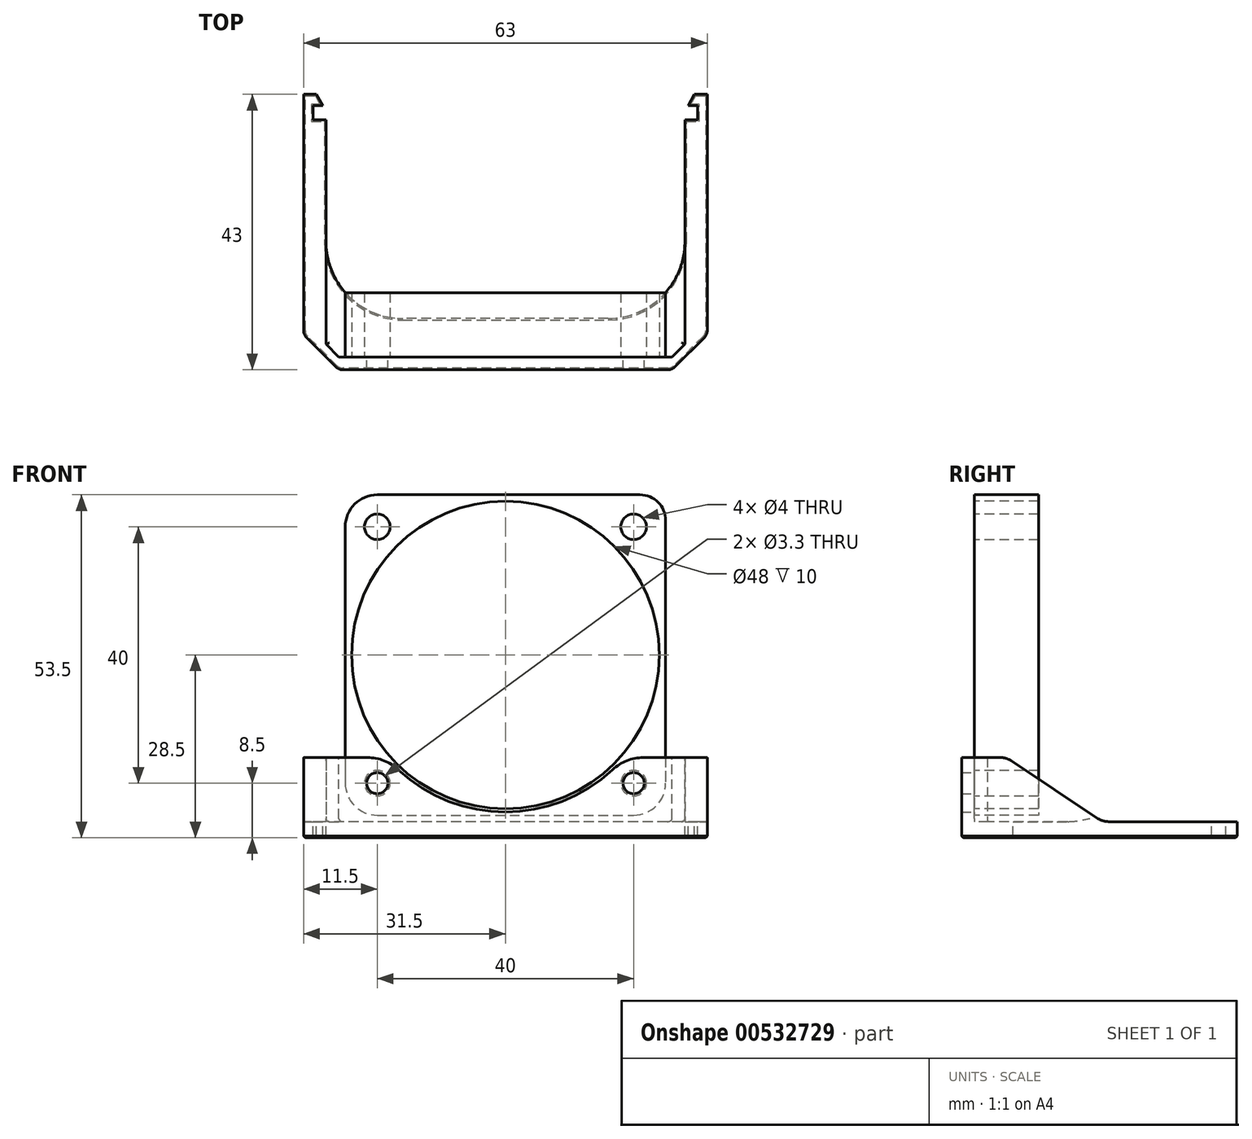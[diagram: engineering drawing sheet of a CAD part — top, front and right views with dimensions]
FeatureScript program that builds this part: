
annotation { "Feature Type Name" : "Feature", "Feature Type Description" : "" }
export const myFeature = defineFeature(function(context is Context, id is Id, definition is map)
    precondition{}
    {
        {
            var Q0;
            Q0=qCreatedBy(makeId("Front.planeOp"),FACE);
            var sketch = newSketch(context, id + "F0", { "sketchPlane" : qUnion([Q0])});
            skLineSegment(sketch, "E0.bottom", {"start": v(-20, 25) * mm, "end": v(21, 25) * mm});
            skLineSegment(sketch, "E0.top", {"start": v(-20, -25) * mm, "end": v(20, -25) * mm});
            skLineSegment(sketch, "E0.left", {"start": v(-25, 20) * mm, "end": v(-25, -20) * mm});
            skLineSegment(sketch, "E0.right", {"start": v(25, 21) * mm, "end": v(25, -20) * mm});
            skPoint(sketch, "E0.middle", {"position": v(0, 0) * mm});
            skCircle(sketch, "E1", {"center": v(20, 20) * mm, "radius": 2 * mm});
            skCircle(sketch, "E2", {"center": v(-20, 20) * mm, "radius": 2 * mm});
            skCircle(sketch, "E3", {"center": v(20, -20) * mm, "radius": 2 * mm});
            skCircle(sketch, "E4", {"center": v(-20, -20) * mm, "radius": 2 * mm});
            skLineSegment(sketch, "E5", {"start": v(20, 20) * mm, "end": v(-20, -20) * mm, "construction": true});
            skLineSegment(sketch, "E6", {"start": v(-20, 20) * mm, "end": v(20, -20) * mm, "construction": true});
            skPoint(sketch, "E7.visualSharp", {"position": v(-25, 25) * mm});
            skArc(sketch, "E7.filletArc", {"start": v(-20, 25) * mm, "mid": v(-23.54, 23.54) * mm, "end": v(-25, 20) * mm});
            skPoint(sketch, "E8.visualSharp", {"position": v(-25, -25) * mm});
            skArc(sketch, "E8.filletArc", {"start": v(-25, -20) * mm, "mid": v(-23.54, -23.54) * mm, "end": v(-20, -25) * mm});
            skPoint(sketch, "E9.visualSharp", {"position": v(25, -25) * mm});
            skArc(sketch, "E9.filletArc", {"start": v(20, -25) * mm, "mid": v(23.54, -23.54) * mm, "end": v(25, -20) * mm});
            skPoint(sketch, "E10.visualSharp", {"position": v(25, 25) * mm});
            skArc(sketch, "E10.filletArc", {"start": v(25, 21) * mm, "mid": v(23.83, 23.83) * mm, "end": v(21, 25) * mm});
            skCircle(sketch, "E11", {"center": v(0, 0) * mm, "radius": 24 * mm});
            skSolve(sketch);
        }
        {
            var Q0;
            Q0=makeQuery(id+"F0.imprint","IMPRINT",FACE,{"disambiguationData":[TD([[makeQuery(id+"F0.imprint","IMPRINT",EDGE,{"derivedFrom":sQuery(id+"F0.wireOp",EDGE,"E0.bottom")}),-1.0]])]});
            extrude(context, id + "F1", {"entities" : qUnion([Q0]), "oppositeDirection" : true, "depth" : 10 * mm, "offsetDistance" : 25 * mm});
        }
        {
            var Q0;
            Q0=makeQuery(id+"F0.imprint","IMPRINT",FACE,{"disambiguationData":[TD([[makeQuery(id+"F0.imprint","IMPRINT",EDGE,{"derivedFrom":sQuery(id+"F0.wireOp",EDGE,"E11")}),1.0]])]});
            var sketch = newSketch(context, id + "F2", { "sketchPlane" : qUnion([Q0])});
            skLineSegment(sketch, "E12", {"start": v(26, -26) * mm, "end": v(-26, -26) * mm});
            skLineSegment(sketch, "E13", {"start": v(-26, -26) * mm, "end": v(-26, -16) * mm});
            skLineSegment(sketch, "E14", {"start": v(26, -26) * mm, "end": v(26, -16) * mm});
            skPoint(sketch, "E15", {"position": v(0, -26) * mm});
            skLineSegment(sketch, "E16", {"start": v(-26, -16) * mm, "end": v(-18.55, -16) * mm});
            skLineSegment(sketch, "E17", {"start": v(26, -16) * mm, "end": v(18.55, -16) * mm});
            skArc(sketch, "E18", {"start": v(-18.55, -16) * mm, "mid": v(0, -24.5) * mm, "end": v(18.55, -16) * mm});
            skArc(sketch, "E19", {"start": v(18.55, -16) * mm, "mid": v(0, 24.5) * mm, "end": v(-18.55, -16) * mm, "construction": true});
            skCircle(sketch, "E20", {"center": v(-20, -20) * mm, "radius": 1.65 * mm});
            skCircle(sketch, "E21", {"center": v(20, -20) * mm, "radius": 1.65 * mm});
            skSolve(sketch);
        }
        {
            var Q0;
            Q0 = qSketchRegion(id + "F2", true);
            extrude(context, id + "F3", {"entities" : qUnion([Q0]), "depth" : 2 * mm, "offsetDistance" : 25 * mm});
        }
        {
            var Q0;
            Q0=makeQuery(id+"F3.opExtrude","SWEPT_FACE",FACE,{"disambiguationData":[OSD([sQuery(id+"F2.wireOp",EDGE,"E12")])]});
            var sketch = newSketch(context, id + "F4", { "sketchPlane" : qUnion([Q0])});
            skLineSegment(sketch, "E22", {"start": v(-31.5, -37) * mm, "end": v(-31.5, -3.5) * mm});
            skLineSegment(sketch, "E23", {"start": v(0, 0) * mm, "end": v(0, -40.2) * mm, "construction": true});
            skLineSegment(sketch, "E24", {"start": v(0, 2) * mm, "end": v(0, -6) * mm});
            skLineSegment(sketch, "E25", {"start": v(0, -6) * mm, "end": v(-16, -6) * mm});
            skLineSegment(sketch, "E26", {"start": v(-28, -18) * mm, "end": v(-28, -37) * mm});
            skLineSegment(sketch, "E27", {"start": v(-26, 2) * mm, "end": v(-31.5, -3.5) * mm});
            skLineSegment(sketch, "E28", {"start": v(-31.5, -37) * mm, "end": v(-31.5, -41) * mm});
            skLineSegment(sketch, "E29", {"start": v(-31.5, -41) * mm, "end": v(-29.5, -41) * mm});
            skLineSegment(sketch, "E30", {"start": v(-29.5, -41) * mm, "end": v(-28.5, -39.2) * mm});
            skLineSegment(sketch, "E31", {"start": v(-28.5, -39.2) * mm, "end": v(-30, -39.2) * mm});
            skLineSegment(sketch, "E32", {"start": v(-30, -39.2) * mm, "end": v(-30, -37) * mm});
            skLineSegment(sketch, "E33", {"start": v(-30, -37) * mm, "end": v(-28, -37) * mm});
            skPoint(sketch, "E34.visualSharp", {"position": v(-28, -6) * mm});
            skArc(sketch, "E34.filletArc", {"start": v(-16, -6) * mm, "mid": v(-24.49, -9.51) * mm, "end": v(-28, -18) * mm});
            skLineSegment(sketch, "E35", {"start": v(-26, 2) * mm, "end": v(0, 2) * mm});
            skPoint(sketch, "E36.orphan", {"position": v(-31.5, 2) * mm});
            skLineSegment(sketch, "E37.MirrorCS", {"start": v(29.5, -41) * mm, "end": v(28.5, -39.2) * mm});
            skLineSegment(sketch, "E38.MirrorCS", {"start": v(31.5, -41) * mm, "end": v(29.5, -41) * mm});
            skLineSegment(sketch, "E39.MirrorCS", {"start": v(30, -37) * mm, "end": v(28, -37) * mm});
            skLineSegment(sketch, "E40.MirrorCS", {"start": v(28.5, -39.2) * mm, "end": v(30, -39.2) * mm});
            skLineSegment(sketch, "E41.MirrorCS", {"start": v(30, -39.2) * mm, "end": v(30, -37) * mm});
            skLineSegment(sketch, "E42.MirrorCS", {"start": v(31.5, -37) * mm, "end": v(31.5, -3.5) * mm});
            skPoint(sketch, "E43.MirrorP", {"position": v(31.5, 2) * mm});
            skLineSegment(sketch, "E44.MirrorCS", {"start": v(0, -6) * mm, "end": v(16, -6) * mm});
            skPoint(sketch, "E45.MirrorP", {"position": v(28, -6) * mm});
            skLineSegment(sketch, "E46.MirrorCS", {"start": v(26, 2) * mm, "end": v(31.5, -3.5) * mm});
            skLineSegment(sketch, "E47.MirrorCS", {"start": v(26, 2) * mm, "end": v(0, 2) * mm});
            skLineSegment(sketch, "E48.MirrorCS", {"start": v(28, -18) * mm, "end": v(28, -37) * mm});
            skLineSegment(sketch, "E49.MirrorCS", {"start": v(31.5, -37) * mm, "end": v(31.5, -41) * mm});
            skArc(sketch, "E50.MirrorCS", {"start": v(16, -6) * mm, "mid": v(24.49, -9.51) * mm, "end": v(28, -18) * mm});
            skSolve(sketch);
        }
        {
            var Q0;
            Q0 = qSketchRegion(id + "F4", true);
            extrude(context, id + "F5", {"entities" : qUnion([Q0]), "operationType" : NewBodyOperationType.ADD, "depth" : 2.5 * mm, "offsetDistance" : 25 * mm});
        }
        {
            var Q0;
            Q0=makeQuery(id+"F4.imprint","IMPRINT",FACE,{"disambiguationData":[TD([[makeQuery(id+"F4.imprint","IMPRINT",EDGE,{"derivedFrom":sQuery(id+"F4.wireOp",EDGE,"E37.MirrorCS")}),-1.0]])]});
            var sketch = newSketch(context, id + "F6", { "sketchPlane" : qUnion([Q0])});
            skLineSegment(sketch, "E51", {"start": v(-26, 2) * mm, "end": v(-31.5, -3.5) * mm});
            skLineSegment(sketch, "E52", {"start": v(-31.5, -3.5) * mm, "end": v(-31.5, -20) * mm});
            skLineSegment(sketch, "E53", {"start": v(-31.5, -20) * mm, "end": v(-28, -20) * mm});
            skLineSegment(sketch, "E54", {"start": v(-28, -20) * mm, "end": v(-28, -2) * mm});
            skLineSegment(sketch, "E55", {"start": v(-28, -2) * mm, "end": v(-26, 0) * mm});
            skLineSegment(sketch, "E56", {"start": v(-26, 0) * mm, "end": v(-26, 2) * mm});
            skLineSegment(sketch, "E57.MirrorCS", {"start": v(26, 0) * mm, "end": v(26, 2) * mm});
            skLineSegment(sketch, "E58.MirrorCS", {"start": v(28, -2) * mm, "end": v(26, 0) * mm});
            skLineSegment(sketch, "E59.MirrorCS", {"start": v(26, 2) * mm, "end": v(31.5, -3.5) * mm});
            skLineSegment(sketch, "E60.MirrorCS", {"start": v(31.5, -20) * mm, "end": v(28, -20) * mm});
            skLineSegment(sketch, "E61.MirrorCS", {"start": v(28, -20) * mm, "end": v(28, -2) * mm});
            skLineSegment(sketch, "E62.MirrorCS", {"start": v(31.5, -3.5) * mm, "end": v(31.5, -20) * mm});
            skSolve(sketch);
        }
        {
            var Q0;
            Q0=makeQuery(id+"F6.imprint","IMPRINT",FACE,{"disambiguationData":[TD([[makeQuery(id+"F6.imprint","IMPRINT",EDGE,{"derivedFrom":sQuery(id+"F6.wireOp",EDGE,"E57.MirrorCS")}),1.0]])]});
            var Q1;
            Q1=makeQuery(id+"F6.imprint","IMPRINT",FACE,{"disambiguationData":[TD([[makeQuery(id+"F6.imprint","IMPRINT",EDGE,{"derivedFrom":sQuery(id+"F6.wireOp",EDGE,"E51")}),1.0]])]});
            var Q2;
            Q2=makeQuery(id+"F3.opExtrude","SWEPT_FACE",FACE,{"disambiguationData":[OSD([sQuery(id+"F2.wireOp",EDGE,"E17")])]});
            extrude(context, id + "F7", {"entities" : qUnion([Q0, Q1]), "operationType" : NewBodyOperationType.ADD, "endBound" : BoundingType.UP_TO_SURFACE, "oppositeDirection" : true, "depth" : 25 * mm, "endBoundEntityFace" : qUnion([Q2]), "offsetDistance" : 25 * mm});
        }
        {
            var Q0;
            Q0=makeQuery(id+"F7.opExtrude","CAP_EDGE",EDGE,{"disambiguationData":[OSD([sQuery(id+"F6.wireOp",EDGE,"E60.MirrorCS")])],"isStart":false});
            chamfer(context, id + "F8", {"entities" : qUnion([Q0]), "chamferType" : ChamferType.TWO_OFFSETS, "width1" : 10 * mm, "oppositeDirection" : false, "width2" : 15 * mm, "tangentPropagation" : true});
        }
        {
            var Q0;
            Q0=makeQuery(id+"F7.opExtrude","CAP_EDGE",EDGE,{"disambiguationData":[OSD([sQuery(id+"F6.wireOp",EDGE,"E53")])],"isStart":false});
            chamfer(context, id + "F9", {"entities" : qUnion([Q0]), "chamferType" : ChamferType.TWO_OFFSETS, "width1" : 15 * mm, "oppositeDirection" : false, "width2" : 10 * mm, "tangentPropagation" : true});
        }
        {
            var Q0;
            {var subQ0=sQuery(id+"F4.wireOp",EDGE,"E29");var subQ1=sQuery(id+"F4.wireOp",EDGE,"E26");var subQ2=sQuery(id+"F4.wireOp",EDGE,"E30");var subQ3=sQuery(id+"F4.wireOp",EDGE,"E28");var subQ4=sQuery(id+"F4.wireOp",EDGE,"E22");var subQ5=sQuery(id+"F4.wireOp",EDGE,"E31");var subQ6=sQuery(id+"F4.wireOp",EDGE,"E32");var subQ7=sQuery(id+"F6.wireOp",EDGE,"E53");var subQ8=sQuery(id+"F4.wireOp",EDGE,"E33");Q0=makeQuery(id+"F9.opChamfer","BLEND_EDGE",EDGE,{"blendedFrom":[makeQuery(id+"F7.opExtrude","CAP_EDGE",EDGE,{"disambiguationData":[OSD([subQ7])],"isStart":false}),makeQuery(id+"F7.boolean.opBoolean","SPLIT",FACE,{"disambiguationData":[TD([makeQuery(id+"F5.opExtrude","SWEPT_FACE",FACE,{"disambiguationData":[OSD([subQ0])]})])],"derivedFrom":makeQuery(id+"F5.opExtrude","CAP_FACE",FACE,{"disambiguationData":[OSD([subQ4,sQuery(id+"F4.wireOp",EDGE,"E25"),subQ1,sQuery(id+"F4.wireOp",EDGE,"E27"),subQ3,subQ0,subQ2,subQ5,subQ6,subQ8,sQuery(id+"F4.wireOp",EDGE,"E34.filletArc"),sQuery(id+"F4.wireOp",EDGE,"E35"),sQuery(id+"F4.wireOp",EDGE,"E37.MirrorCS"),sQuery(id+"F4.wireOp",EDGE,"E38.MirrorCS"),sQuery(id+"F4.wireOp",EDGE,"E39.MirrorCS"),sQuery(id+"F4.wireOp",EDGE,"E40.MirrorCS"),sQuery(id+"F4.wireOp",EDGE,"E41.MirrorCS"),sQuery(id+"F4.wireOp",EDGE,"E42.MirrorCS"),sQuery(id+"F4.wireOp",EDGE,"E44.MirrorCS"),sQuery(id+"F4.wireOp",EDGE,"E46.MirrorCS"),sQuery(id+"F4.wireOp",EDGE,"E47.MirrorCS"),sQuery(id+"F4.wireOp",EDGE,"E48.MirrorCS"),sQuery(id+"F4.wireOp",EDGE,"E49.MirrorCS"),sQuery(id+"F4.wireOp",EDGE,"E50.MirrorCS")])],"isStart":true})})],"blendedInto":[makeQuery(id+"F7.boolean.opBoolean","SPLIT",FACE,{"disambiguationData":[TD([makeQuery(id+"F5.opExtrude","SWEPT_FACE",FACE,{"disambiguationData":[OSD([subQ0])]})])],"derivedFrom":makeQuery(id+"F5.opExtrude","CAP_FACE",FACE,{"disambiguationData":[OSD([subQ4,sQuery(id+"F4.wireOp",EDGE,"E25"),subQ1,sQuery(id+"F4.wireOp",EDGE,"E27"),subQ3,subQ0,subQ2,subQ5,subQ6,subQ8,sQuery(id+"F4.wireOp",EDGE,"E34.filletArc"),sQuery(id+"F4.wireOp",EDGE,"E35"),sQuery(id+"F4.wireOp",EDGE,"E37.MirrorCS"),sQuery(id+"F4.wireOp",EDGE,"E38.MirrorCS"),sQuery(id+"F4.wireOp",EDGE,"E39.MirrorCS"),sQuery(id+"F4.wireOp",EDGE,"E40.MirrorCS"),sQuery(id+"F4.wireOp",EDGE,"E41.MirrorCS"),sQuery(id+"F4.wireOp",EDGE,"E42.MirrorCS"),sQuery(id+"F4.wireOp",EDGE,"E44.MirrorCS"),sQuery(id+"F4.wireOp",EDGE,"E46.MirrorCS"),sQuery(id+"F4.wireOp",EDGE,"E47.MirrorCS"),sQuery(id+"F4.wireOp",EDGE,"E48.MirrorCS"),sQuery(id+"F4.wireOp",EDGE,"E49.MirrorCS"),sQuery(id+"F4.wireOp",EDGE,"E50.MirrorCS")])],"isStart":true})})]});}
            var Q1;
            {var subQ0=sQuery(id+"F4.wireOp",EDGE,"E40.MirrorCS");var subQ1=sQuery(id+"F4.wireOp",EDGE,"E39.MirrorCS");var subQ2=sQuery(id+"F4.wireOp",EDGE,"E38.MirrorCS");var subQ3=sQuery(id+"F4.wireOp",EDGE,"E37.MirrorCS");var subQ4=sQuery(id+"F4.wireOp",EDGE,"E41.MirrorCS");var subQ5=sQuery(id+"F4.wireOp",EDGE,"E49.MirrorCS");var subQ6=sQuery(id+"F4.wireOp",EDGE,"E42.MirrorCS");var subQ7=sQuery(id+"F6.wireOp",EDGE,"E60.MirrorCS");var subQ8=sQuery(id+"F4.wireOp",EDGE,"E48.MirrorCS");Q1=makeQuery(id+"F8.opChamfer","BLEND_EDGE",EDGE,{"blendedFrom":[makeQuery(id+"F7.opExtrude","CAP_EDGE",EDGE,{"disambiguationData":[OSD([subQ7])],"isStart":false}),makeQuery(id+"F7.boolean.opBoolean","SPLIT",FACE,{"disambiguationData":[TD([makeQuery(id+"F5.opExtrude","SWEPT_FACE",FACE,{"disambiguationData":[OSD([subQ3])]})])],"derivedFrom":makeQuery(id+"F5.opExtrude","CAP_FACE",FACE,{"disambiguationData":[OSD([sQuery(id+"F4.wireOp",EDGE,"E22"),sQuery(id+"F4.wireOp",EDGE,"E25"),sQuery(id+"F4.wireOp",EDGE,"E26"),sQuery(id+"F4.wireOp",EDGE,"E27"),sQuery(id+"F4.wireOp",EDGE,"E28"),sQuery(id+"F4.wireOp",EDGE,"E29"),sQuery(id+"F4.wireOp",EDGE,"E30"),sQuery(id+"F4.wireOp",EDGE,"E31"),sQuery(id+"F4.wireOp",EDGE,"E32"),sQuery(id+"F4.wireOp",EDGE,"E33"),sQuery(id+"F4.wireOp",EDGE,"E34.filletArc"),sQuery(id+"F4.wireOp",EDGE,"E35"),subQ3,subQ2,subQ1,subQ0,subQ4,subQ6,sQuery(id+"F4.wireOp",EDGE,"E44.MirrorCS"),sQuery(id+"F4.wireOp",EDGE,"E46.MirrorCS"),sQuery(id+"F4.wireOp",EDGE,"E47.MirrorCS"),subQ8,subQ5,sQuery(id+"F4.wireOp",EDGE,"E50.MirrorCS")])],"isStart":true})})],"blendedInto":[makeQuery(id+"F7.boolean.opBoolean","SPLIT",FACE,{"disambiguationData":[TD([makeQuery(id+"F5.opExtrude","SWEPT_FACE",FACE,{"disambiguationData":[OSD([subQ3])]})])],"derivedFrom":makeQuery(id+"F5.opExtrude","CAP_FACE",FACE,{"disambiguationData":[OSD([sQuery(id+"F4.wireOp",EDGE,"E22"),sQuery(id+"F4.wireOp",EDGE,"E25"),sQuery(id+"F4.wireOp",EDGE,"E26"),sQuery(id+"F4.wireOp",EDGE,"E27"),sQuery(id+"F4.wireOp",EDGE,"E28"),sQuery(id+"F4.wireOp",EDGE,"E29"),sQuery(id+"F4.wireOp",EDGE,"E30"),sQuery(id+"F4.wireOp",EDGE,"E31"),sQuery(id+"F4.wireOp",EDGE,"E32"),sQuery(id+"F4.wireOp",EDGE,"E33"),sQuery(id+"F4.wireOp",EDGE,"E34.filletArc"),sQuery(id+"F4.wireOp",EDGE,"E35"),subQ3,subQ2,subQ1,subQ0,subQ4,subQ6,sQuery(id+"F4.wireOp",EDGE,"E44.MirrorCS"),sQuery(id+"F4.wireOp",EDGE,"E46.MirrorCS"),sQuery(id+"F4.wireOp",EDGE,"E47.MirrorCS"),subQ8,subQ5,sQuery(id+"F4.wireOp",EDGE,"E50.MirrorCS")])],"isStart":true})})]});}
            var Q2;
            {var subQ0=sQuery(id+"F6.wireOp",EDGE,"E60.MirrorCS");Q2=makeQuery(id+"F8.opChamfer","BLEND_EDGE",EDGE,{"blendedFrom":[makeQuery(id+"F7.opExtrude","CAP_EDGE",EDGE,{"disambiguationData":[OSD([subQ0])],"isStart":false}),makeQuery(id+"F7.boolean.opBoolean","MERGE",FACE,{"derivedFrom":[makeQuery(id+"F3.opExtrude","SWEPT_FACE",FACE,{"disambiguationData":[OSD([sQuery(id+"F2.wireOp",EDGE,"E17")])]}),makeQuery(id+"F7.opExtrude","CAP_FACE",FACE,{"disambiguationData":[OSD([sQuery(id+"F6.wireOp",EDGE,"E57.MirrorCS"),sQuery(id+"F6.wireOp",EDGE,"E58.MirrorCS"),sQuery(id+"F6.wireOp",EDGE,"E59.MirrorCS"),subQ0,sQuery(id+"F6.wireOp",EDGE,"E61.MirrorCS"),sQuery(id+"F6.wireOp",EDGE,"E62.MirrorCS")])],"isStart":false})]})],"blendedInto":[makeQuery(id+"F7.boolean.opBoolean","MERGE",FACE,{"derivedFrom":[makeQuery(id+"F3.opExtrude","SWEPT_FACE",FACE,{"disambiguationData":[OSD([sQuery(id+"F2.wireOp",EDGE,"E17")])]}),makeQuery(id+"F7.opExtrude","CAP_FACE",FACE,{"disambiguationData":[OSD([sQuery(id+"F6.wireOp",EDGE,"E57.MirrorCS"),sQuery(id+"F6.wireOp",EDGE,"E58.MirrorCS"),sQuery(id+"F6.wireOp",EDGE,"E59.MirrorCS"),subQ0,sQuery(id+"F6.wireOp",EDGE,"E61.MirrorCS"),sQuery(id+"F6.wireOp",EDGE,"E62.MirrorCS")])],"isStart":false})]})]});}
            var Q3;
            {var subQ0=sQuery(id+"F6.wireOp",EDGE,"E53");Q3=makeQuery(id+"F9.opChamfer","BLEND_EDGE",EDGE,{"blendedFrom":[makeQuery(id+"F7.opExtrude","CAP_EDGE",EDGE,{"disambiguationData":[OSD([subQ0])],"isStart":false}),makeQuery(id+"F7.boolean.opBoolean","MERGE",FACE,{"derivedFrom":[makeQuery(id+"F3.opExtrude","SWEPT_FACE",FACE,{"disambiguationData":[OSD([sQuery(id+"F2.wireOp",EDGE,"E16")])]}),makeQuery(id+"F7.opExtrude","CAP_FACE",FACE,{"disambiguationData":[OSD([sQuery(id+"F6.wireOp",EDGE,"E51"),sQuery(id+"F6.wireOp",EDGE,"E52"),subQ0,sQuery(id+"F6.wireOp",EDGE,"E54"),sQuery(id+"F6.wireOp",EDGE,"E55"),sQuery(id+"F6.wireOp",EDGE,"E56")])],"isStart":false})]})],"blendedInto":[makeQuery(id+"F7.boolean.opBoolean","MERGE",FACE,{"derivedFrom":[makeQuery(id+"F3.opExtrude","SWEPT_FACE",FACE,{"disambiguationData":[OSD([sQuery(id+"F2.wireOp",EDGE,"E16")])]}),makeQuery(id+"F7.opExtrude","CAP_FACE",FACE,{"disambiguationData":[OSD([sQuery(id+"F6.wireOp",EDGE,"E51"),sQuery(id+"F6.wireOp",EDGE,"E52"),subQ0,sQuery(id+"F6.wireOp",EDGE,"E54"),sQuery(id+"F6.wireOp",EDGE,"E55"),sQuery(id+"F6.wireOp",EDGE,"E56")])],"isStart":false})]})]});}
            fillet(context, id + "F10", {"entities" : qUnion([Q0, Q1, Q2, Q3]), "tangentPropagation" : true, "radius" : 3 * mm, "defaultsChanged" : true, "vertexSettings" : [], "allowEdgeOverflow" : false});
        }
        {
            var Q0;
            Q0=makeQuery(id+"F3.opExtrude","SWEPT_EDGE",EDGE,{"disambiguationData":[OSD([sQuery(id+"F2.wireOp",EDGE,"E17"),sQuery(id+"F2.wireOp",EDGE,"E18")])]});
            var Q1;
            Q1=makeQuery(id+"F3.opExtrude","SWEPT_EDGE",EDGE,{"disambiguationData":[OSD([sQuery(id+"F2.wireOp",EDGE,"E16"),sQuery(id+"F2.wireOp",EDGE,"E18")])]});
            fillet(context, id + "F11", {"entities" : qUnion([Q0, Q1]), "tangentPropagation" : true, "radius" : 7 * mm, "defaultsChanged" : true, "vertexSettings" : [], "allowEdgeOverflow" : false});
        }
        {
            var Q0;
            Q0=makeQuery(id+"F7.boolean.opBoolean","MERGE",EDGE,{"derivedFrom":[makeQuery(id+"F5.opExtrude","SWEPT_EDGE",EDGE,{"disambiguationData":[OSD([sQuery(id+"F4.wireOp",EDGE,"E22"),sQuery(id+"F4.wireOp",EDGE,"E27")])]}),makeQuery(id+"F7.opExtrude","SWEPT_EDGE",EDGE,{"disambiguationData":[OSD([sQuery(id+"F6.wireOp",EDGE,"E51"),sQuery(id+"F6.wireOp",EDGE,"E52")])]})]});
            var Q1;
            {var subQ0=sQuery(id+"F2.wireOp",EDGE,"E13");Q1=makeQuery(id+"F7.boolean.opBoolean","MERGE",EDGE,{"derivedFrom":[makeQuery(id+"F3.opExtrude","CAP_EDGE",EDGE,{"disambiguationData":[OSD([subQ0])],"isStart":false}),makeQuery(id+"F5.opExtrude","SWEPT_EDGE",EDGE,{"disambiguationData":[OSD([sQuery(id+"F2.wireOp",EDGE,"E12"),subQ0,sQuery(id+"F4.wireOp",EDGE,"E27"),sQuery(id+"F4.wireOp",EDGE,"E35")])]}),makeQuery(id+"F7.opExtrude","SWEPT_EDGE",EDGE,{"disambiguationData":[OSD([sQuery(id+"F6.wireOp",EDGE,"E51"),sQuery(id+"F6.wireOp",EDGE,"E56")])]})]});}
            var Q2;
            Q2=makeQuery(id+"F7.boolean.opBoolean","MERGE",EDGE,{"derivedFrom":[makeQuery(id+"F5.opExtrude","SWEPT_EDGE",EDGE,{"disambiguationData":[OSD([sQuery(id+"F4.wireOp",EDGE,"E42.MirrorCS"),sQuery(id+"F4.wireOp",EDGE,"E46.MirrorCS")])]}),makeQuery(id+"F7.opExtrude","SWEPT_EDGE",EDGE,{"disambiguationData":[OSD([sQuery(id+"F6.wireOp",EDGE,"E59.MirrorCS"),sQuery(id+"F6.wireOp",EDGE,"E62.MirrorCS")])]})]});
            var Q3;
            {var subQ0=sQuery(id+"F2.wireOp",EDGE,"E14");Q3=makeQuery(id+"F7.boolean.opBoolean","MERGE",EDGE,{"derivedFrom":[makeQuery(id+"F3.opExtrude","CAP_EDGE",EDGE,{"disambiguationData":[OSD([subQ0])],"isStart":false}),makeQuery(id+"F5.opExtrude","SWEPT_EDGE",EDGE,{"disambiguationData":[OSD([sQuery(id+"F2.wireOp",EDGE,"E12"),subQ0,sQuery(id+"F4.wireOp",EDGE,"E46.MirrorCS"),sQuery(id+"F4.wireOp",EDGE,"E47.MirrorCS")])]}),makeQuery(id+"F7.opExtrude","SWEPT_EDGE",EDGE,{"disambiguationData":[OSD([sQuery(id+"F6.wireOp",EDGE,"E57.MirrorCS"),sQuery(id+"F6.wireOp",EDGE,"E59.MirrorCS")])]})]});}
            fillet(context, id + "F12", {"entities" : qUnion([Q0, Q1, Q2, Q3]), "tangentPropagation" : true, "radius" : 1.5 * mm, "defaultsChanged" : true, "vertexSettings" : [], "allowEdgeOverflow" : false});
        }
        {
            var Q0;
            Q0=makeQuery(id+"F7.opExtrude","CAP_EDGE",EDGE,{"disambiguationData":[OSD([sQuery(id+"F6.wireOp",EDGE,"E61.MirrorCS")])],"isStart":true});
            var Q1;
            Q1=makeQuery(id+"F7.opExtrude","CAP_EDGE",EDGE,{"disambiguationData":[OSD([sQuery(id+"F6.wireOp",EDGE,"E58.MirrorCS")])],"isStart":true});
            var Q2;
            Q2=makeQuery(id+"F3.opExtrude","CAP_EDGE",EDGE,{"disambiguationData":[OSD([sQuery(id+"F2.wireOp",EDGE,"E12")])],"isStart":true});
            var Q3;
            Q3=makeQuery(id+"F7.opExtrude","CAP_EDGE",EDGE,{"disambiguationData":[OSD([sQuery(id+"F6.wireOp",EDGE,"E55")])],"isStart":true});
            var Q4;
            Q4=makeQuery(id+"F7.opExtrude","CAP_EDGE",EDGE,{"disambiguationData":[OSD([sQuery(id+"F6.wireOp",EDGE,"E54")])],"isStart":true});
            fillet(context, id + "F13", {"entities" : qUnion([Q0, Q1, Q2, Q3, Q4]), "tangentPropagation" : true, "radius" : 0.5 * mm, "defaultsChanged" : false, "vertexSettings" : [], "allowEdgeOverflow" : false});
        }
        {
            var Q0;
            Q0=makeQuery(id+"F5.opExtrude","CAP_FACE",FACE,{"disambiguationData":[OSD([sQuery(id+"F4.wireOp",EDGE,"E22"),sQuery(id+"F4.wireOp",EDGE,"E25"),sQuery(id+"F4.wireOp",EDGE,"E26"),sQuery(id+"F4.wireOp",EDGE,"E27"),sQuery(id+"F4.wireOp",EDGE,"E28"),sQuery(id+"F4.wireOp",EDGE,"E29"),sQuery(id+"F4.wireOp",EDGE,"E30"),sQuery(id+"F4.wireOp",EDGE,"E31"),sQuery(id+"F4.wireOp",EDGE,"E32"),sQuery(id+"F4.wireOp",EDGE,"E33"),sQuery(id+"F4.wireOp",EDGE,"E34.filletArc"),sQuery(id+"F4.wireOp",EDGE,"E35"),sQuery(id+"F4.wireOp",EDGE,"E37.MirrorCS"),sQuery(id+"F4.wireOp",EDGE,"E38.MirrorCS"),sQuery(id+"F4.wireOp",EDGE,"E39.MirrorCS"),sQuery(id+"F4.wireOp",EDGE,"E40.MirrorCS"),sQuery(id+"F4.wireOp",EDGE,"E41.MirrorCS"),sQuery(id+"F4.wireOp",EDGE,"E42.MirrorCS"),sQuery(id+"F4.wireOp",EDGE,"E44.MirrorCS"),sQuery(id+"F4.wireOp",EDGE,"E46.MirrorCS"),sQuery(id+"F4.wireOp",EDGE,"E47.MirrorCS"),sQuery(id+"F4.wireOp",EDGE,"E48.MirrorCS"),sQuery(id+"F4.wireOp",EDGE,"E49.MirrorCS"),sQuery(id+"F4.wireOp",EDGE,"E50.MirrorCS")])],"isStart":false});
            chamfer(context, id + "F14", {"entities" : qUnion([Q0]), "width" : 0.25 * mm, "tangentPropagation" : true});
        }
    });
